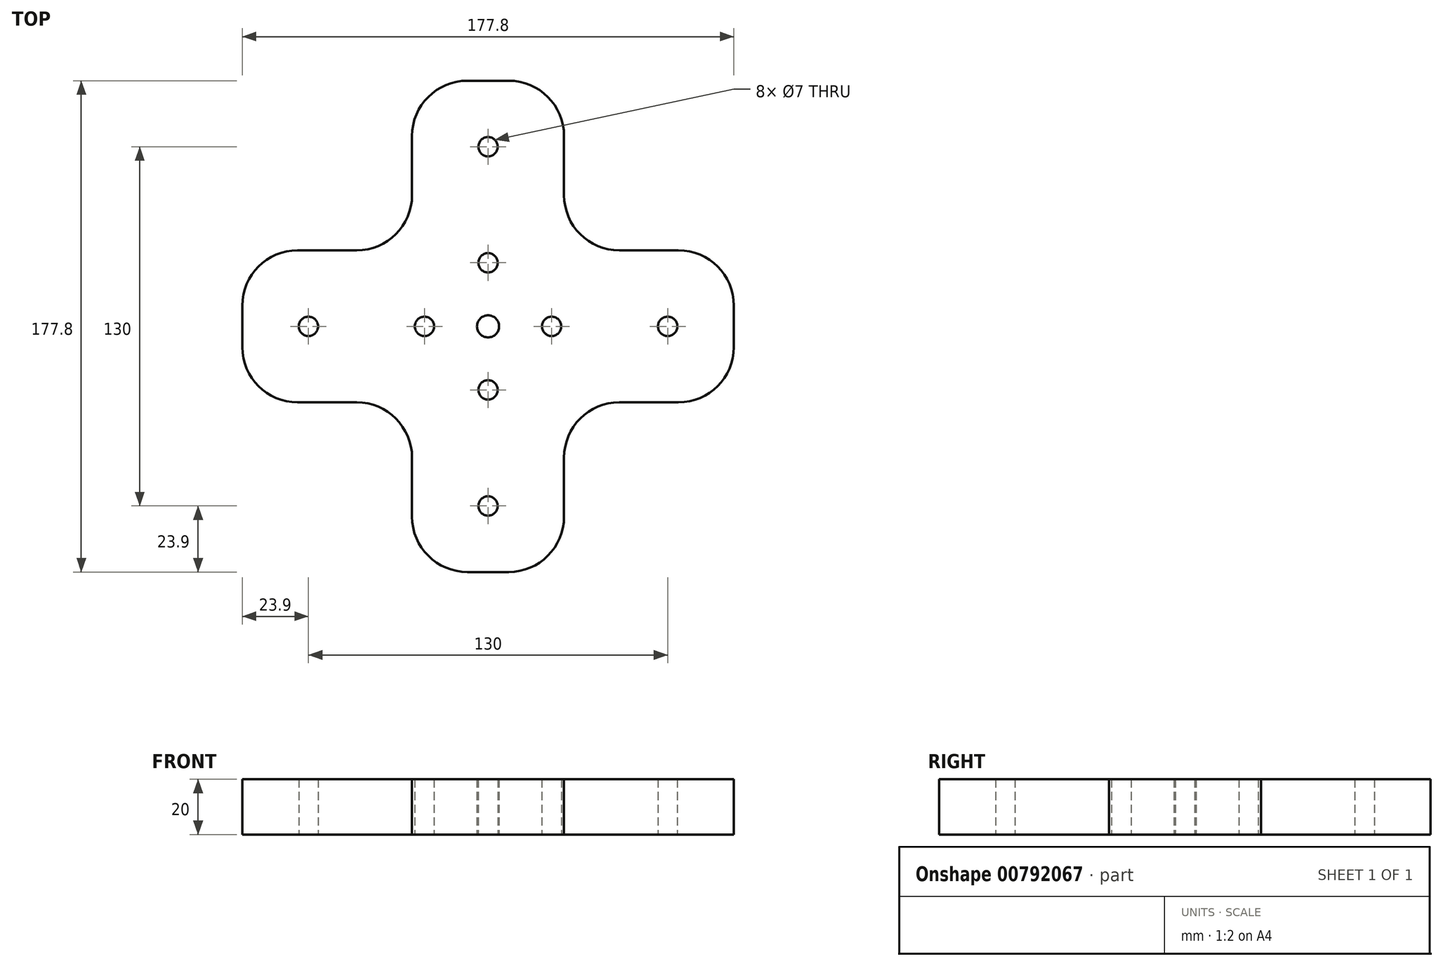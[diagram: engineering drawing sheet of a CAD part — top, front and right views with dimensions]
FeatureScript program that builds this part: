
annotation { "Feature Type Name" : "Feature", "Feature Type Description" : "" }
export const myFeature = defineFeature(function(context is Context, id is Id, definition is map)
    precondition{}
    {
        {
            var Q0;
            Q0=qCreatedBy(makeId("Top.planeOp"),FACE);
            var sketch = newSketch(context, id + "F0", { "sketchPlane" : qUnion([Q0])});
            skLineSegment(sketch, "E0.bottom", {"start": v(27.5, 27.5) * mm, "end": v(68.9, 27.5) * mm});
            skLineSegment(sketch, "E0.top", {"start": v(27.5, -27.5) * mm, "end": v(68.9, -27.5) * mm});
            skLineSegment(sketch, "E0.right", {"start": v(88.9, 7.5) * mm, "end": v(88.9, -7.5) * mm});
            skPoint(sketch, "E1.visualSharp", {"position": v(88.9, 27.5) * mm});
            skArc(sketch, "E1.filletArc", {"start": v(88.9, 7.5) * mm, "mid": v(83.04, 21.64) * mm, "end": v(68.9, 27.5) * mm});
            skPoint(sketch, "E2.visualSharp", {"position": v(88.9, -27.5) * mm});
            skArc(sketch, "E2.filletArc", {"start": v(68.9, -27.5) * mm, "mid": v(83.04, -21.64) * mm, "end": v(88.9, -7.5) * mm});
            skArc(sketch, "E3", {"start": v(0, -4) * mm, "mid": v(4, 0) * mm, "end": v(0, 4) * mm});
            skCircle(sketch, "E4", {"center": v(23, 0) * mm, "radius": 3.5 * mm});
            skCircle(sketch, "E5", {"center": v(65, 0) * mm, "radius": 3.5 * mm});
            skPoint(sketch, "E6.1.0", {"position": v(27.5, 88.9) * mm});
            skLineSegment(sketch, "E6.1.2", {"start": v(-7.5, 88.9) * mm, "end": v(7.5, 88.9) * mm});
            skLineSegment(sketch, "E6.1.3", {"start": v(27.5, 27.5) * mm, "end": v(27.5, 68.9) * mm});
            skCircle(sketch, "E6.1.4", {"center": v(0, 23) * mm, "radius": 3.5 * mm});
            skCircle(sketch, "E6.1.6", {"center": v(0, 65) * mm, "radius": 3.5 * mm});
            skArc(sketch, "E6.1.7", {"start": v(-7.5, 88.9) * mm, "mid": v(-21.64, 83.04) * mm, "end": v(-27.5, 68.9) * mm});
            skPoint(sketch, "E6.1.8", {"position": v(-27.5, 88.9) * mm});
            skLineSegment(sketch, "E6.1.9", {"start": v(-27.5, 27.5) * mm, "end": v(-27.5, 68.9) * mm});
            skArc(sketch, "E6.1.10", {"start": v(27.5, 68.9) * mm, "mid": v(21.64, 83.04) * mm, "end": v(7.5, 88.9) * mm});
            skArc(sketch, "E6.1.11", {"start": v(4, 0) * mm, "mid": v(0, 4) * mm, "end": v(-4, 0) * mm});
            skPoint(sketch, "E6.2.0", {"position": v(-88.9, 27.5) * mm});
            skLineSegment(sketch, "E6.2.2", {"start": v(-88.9, -7.5) * mm, "end": v(-88.9, 7.5) * mm});
            skLineSegment(sketch, "E6.2.3", {"start": v(-27.5, 27.5) * mm, "end": v(-68.9, 27.5) * mm});
            skCircle(sketch, "E6.2.4", {"center": v(-23, 0) * mm, "radius": 3.5 * mm});
            skCircle(sketch, "E6.2.6", {"center": v(-65, 0) * mm, "radius": 3.5 * mm});
            skArc(sketch, "E6.2.7", {"start": v(-88.9, -7.5) * mm, "mid": v(-83.04, -21.64) * mm, "end": v(-68.9, -27.5) * mm});
            skPoint(sketch, "E6.2.8", {"position": v(-88.9, -27.5) * mm});
            skLineSegment(sketch, "E6.2.9", {"start": v(-27.5, -27.5) * mm, "end": v(-68.9, -27.5) * mm});
            skArc(sketch, "E6.2.10", {"start": v(-68.9, 27.5) * mm, "mid": v(-83.04, 21.64) * mm, "end": v(-88.9, 7.5) * mm});
            skArc(sketch, "E6.2.11", {"start": v(0, 4) * mm, "mid": v(-4, 0) * mm, "end": v(0, -4) * mm});
            skPoint(sketch, "E6.3.0", {"position": v(-27.5, -88.9) * mm});
            skLineSegment(sketch, "E6.3.2", {"start": v(7.5, -88.9) * mm, "end": v(-7.5, -88.9) * mm});
            skLineSegment(sketch, "E6.3.3", {"start": v(-27.5, -27.5) * mm, "end": v(-27.5, -68.9) * mm});
            skCircle(sketch, "E6.3.4", {"center": v(0, -23) * mm, "radius": 3.5 * mm});
            skCircle(sketch, "E6.3.6", {"center": v(0, -65) * mm, "radius": 3.5 * mm});
            skArc(sketch, "E6.3.7", {"start": v(7.5, -88.9) * mm, "mid": v(21.64, -83.04) * mm, "end": v(27.5, -68.9) * mm});
            skPoint(sketch, "E6.3.8", {"position": v(27.5, -88.9) * mm});
            skLineSegment(sketch, "E6.3.9", {"start": v(27.5, -27.5) * mm, "end": v(27.5, -68.9) * mm});
            skArc(sketch, "E6.3.10", {"start": v(-27.5, -68.9) * mm, "mid": v(-21.64, -83.04) * mm, "end": v(-7.5, -88.9) * mm});
            skArc(sketch, "E6.3.11", {"start": v(-4, 0) * mm, "mid": v(0, -4) * mm, "end": v(4, 0) * mm});
            skPoint(sketch, "E6.center", {"position": v(8, 0) * mm});
            skPoint(sketch, "E7.orphan", {"position": v(0, 27.5) * mm});
            skPoint(sketch, "E8.orphan", {"position": v(0, -27.5) * mm});
            skPoint(sketch, "E9.orphan", {"position": v(27.5, 0) * mm});
            skPoint(sketch, "E10.orphan", {"position": v(-27.5, 0) * mm});
            skSolve(sketch);
        }
        {
            var Q0;
            Q0 = qSketchRegion(id + "F0", true);
            extrude(context, id + "F1", {"entities" : qUnion([Q0]), "depth" : 20 * mm, "offsetDistance" : 25 * mm});
        }
        {
            var Q0;
            Q0=makeQuery(id+"F1.opExtrude","SWEPT_EDGE",EDGE,{"disambiguationData":[OSD([sQuery(id+"F0.wireOp",EDGE,"E0.bottom"),sQuery(id+"F0.wireOp",EDGE,"E6.1.3")])]});
            var Q1;
            Q1=makeQuery(id+"F1.opExtrude","SWEPT_EDGE",EDGE,{"disambiguationData":[OSD([sQuery(id+"F0.wireOp",EDGE,"E0.top"),sQuery(id+"F0.wireOp",EDGE,"E6.3.9")])]});
            var Q2;
            Q2=makeQuery(id+"F1.opExtrude","SWEPT_EDGE",EDGE,{"disambiguationData":[OSD([sQuery(id+"F0.wireOp",EDGE,"E6.2.9"),sQuery(id+"F0.wireOp",EDGE,"E6.3.3")])]});
            var Q3;
            Q3=makeQuery(id+"F1.opExtrude","SWEPT_EDGE",EDGE,{"disambiguationData":[OSD([sQuery(id+"F0.wireOp",EDGE,"E6.1.9"),sQuery(id+"F0.wireOp",EDGE,"E6.2.3")])]});
            fillet(context, id + "F2", {"entities" : qUnion([Q0, Q1, Q2, Q3]), "radius" : 20 * mm, "tangentPropagation" : true, "allowEdgeOverflow" : false});
        }
    });
